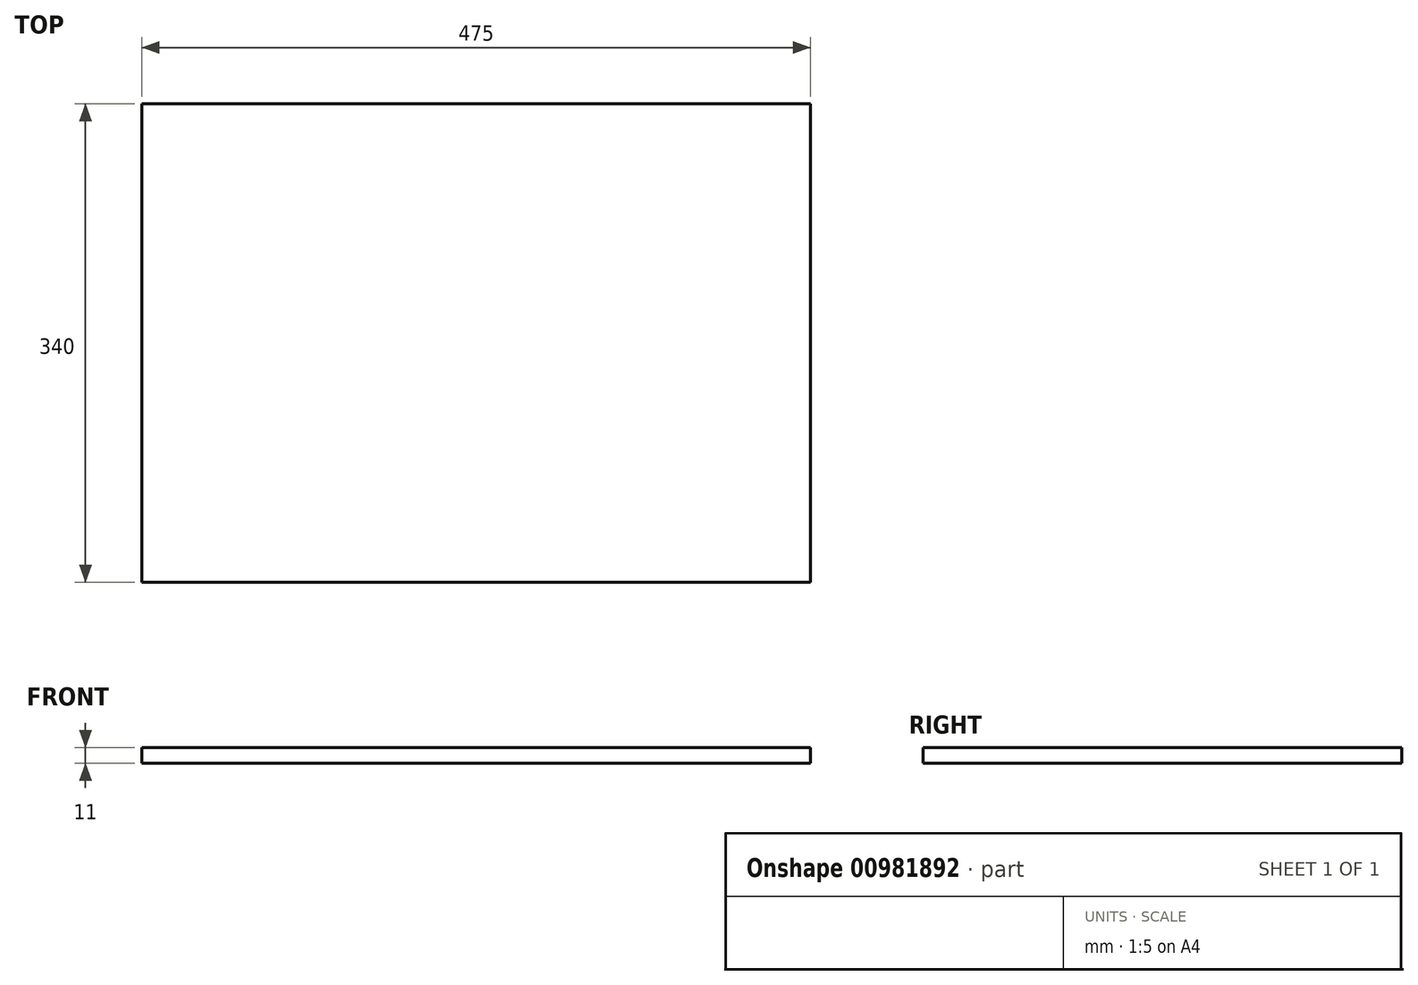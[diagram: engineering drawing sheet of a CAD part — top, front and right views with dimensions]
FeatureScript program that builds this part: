
annotation { "Feature Type Name" : "Feature", "Feature Type Description" : "" }
export const myFeature = defineFeature(function(context is Context, id is Id, definition is map)
    precondition{}
    {
        {
            var Q0;
            Q0=qCreatedBy(makeId("Top.planeOp"),FACE);
            var sketch = newSketch(context, id + "F0", { "sketchPlane" : qUnion([Q0])});
            skLineSegment(sketch, "E0.bottom", {"start": v(-238.7, 246.84) * mm, "end": v(236.3, 246.84) * mm});
            skLineSegment(sketch, "E0.top", {"start": v(-238.7, -93.16) * mm, "end": v(236.3, -93.16) * mm});
            skLineSegment(sketch, "E0.left", {"start": v(-238.7, 246.84) * mm, "end": v(-238.7, -93.16) * mm});
            skLineSegment(sketch, "E0.right", {"start": v(236.3, 246.84) * mm, "end": v(236.3, -93.16) * mm});
            skSolve(sketch);
        }
        {
            var Q0;
            Q0=makeQuery(id+"F0.imprint","IMPRINT",FACE,{"disambiguationData":[TD([[makeQuery(id+"F0.imprint","IMPRINT",EDGE,{"derivedFrom":sQuery(id+"F0.wireOp",EDGE,"E0.bottom")}),-1.0]])]});
            extrude(context, id + "F1", {"entities" : qUnion([Q0]), "depth" : 11 * mm, "offsetDistance" : 25 * mm});
        }
    });
